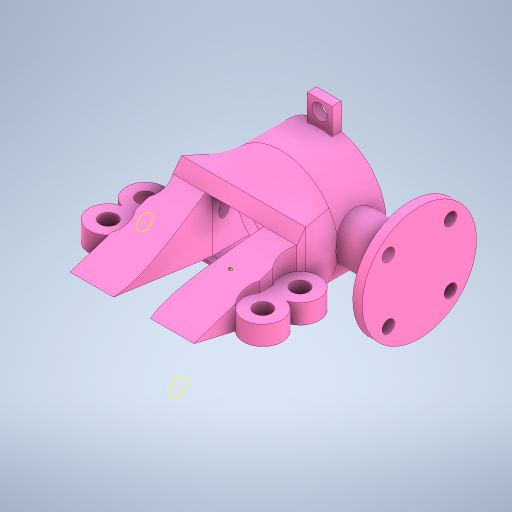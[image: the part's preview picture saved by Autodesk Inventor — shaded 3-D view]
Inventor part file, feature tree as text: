
AUTODESK INVENTOR PART (.ipt)
format: ipt  version: 2024 (Build 280153000, 153)  size: 1,857,024 bytes
history: native  units: mm
features: sketch x24, extrude x19, projected_geometry x11, split x10, other x10, loft x6, boolean_combine x5, plane x4, fillet x2, sweep x2, thicken_offset x2
ambient origin geometry x8: Origin, YZ Plane, XZ Plane, XY Plane, X Axis, Y Axis, Z Axis, Center Point
bodies: Solid1 (feature_tree), Solid2 (feature_tree), Solid19 (feature_tree), Solid20 (feature_tree), Solid21 (feature_tree), Solid22 (feature_tree), Solid23 (feature_tree), Solid3 (feature_tree), Solid4 (feature_tree), Solid5 (feature_tree), Solid6 (feature_tree), Solid7 (feature_tree), Solid8 (feature_tree), Solid9 (feature_tree), Solid10 (feature_tree), Solid11 (feature_tree), Solid12 (feature_tree), Solid13 (feature_tree), Solid14 (feature_tree), Solid15 (feature_tree), Solid16 (feature_tree), Solid17 (feature_tree), Solid18 (feature_tree)
feature tree (95):
  extrude  "Extrusion1"  Depth=3.0mm TaperAngle=0.0deg
  extrude  "Extrusion2"  Depth=3.0mm TaperAngle=0.0deg
  extrude  "Extrusion3"  Depth=40.0mm
  plane  "Work Plane2"
  sketch  "Sketch4"  dims[d4=29.0mm d5=3.0mm d6=0.0mm]
  loft  "Loft1"
  loft  "Loft2"
  loft  "Loft3"
  loft  "Loft4"
  boolean_combine  "Combine1"
  loft  "Loft5"
  fillet  "Fillet1"  [1 undecoded]
  fillet  "Fillet2"  [1 undecoded]
  plane  "Work Plane3"
  extrude  "Extrusion5"  TaperAngle=0.0deg  [1 undecoded]
  extrude  "Extrusion6"  TaperAngle=0.0deg  [1 undecoded]
  extrude  "Extrusion7"  Depth=40.0mm
  extrude  "Extrusion8"  TaperAngle=0.0deg  [1 undecoded]
  extrude  "Extrusion9"  Depth=2.0mm
  extrude  "Extrusion10"  Depth=38.0mm
  extrude  "Extrusion11"  Depth=3.0mm TaperAngle=0.0deg
  extrude  "Extrusion12"  Depth=3.0mm TaperAngle=0.0deg
  extrude  "Extrusion13"  Depth=12.5mm TaperAngle=0.0deg
  extrude  "Extrusion14"  Depth=3.7mm TaperAngle=0.0deg
  extrude  "Extrusion15"  Depth=8.5mm
  split  "Split1"
  split  "Split2"
  split  "Split3"
  split  "Split4"
  split  "Split5"
  split  "Split6"
  split  "Split7"
  boolean_combine  "Combine2"
  split  "Split8"
  boolean_combine  "Combine3"
  boolean_combine  "Combine4"
  extrude  "Extrusion16"  Depth=8.5mm
  extrude  "Extrusion17"  Depth=2.7mm TaperAngle=0.0deg
  sketch  "Sketch36"  dims[d47=15.0mm d48=3.0mm d49=0.0mm]
  sweep  "Sweep1"
  split  "Split9"
  loft  "Loft6"
  thicken_offset  "Thicken1"
  extrude  "Extrusion18"  Depth=10.0mm TaperAngle=0.0deg
  sweep  "Sweep2"
  split  "Split10"
  thicken_offset  "Thicken2"
  boolean_combine  "Combine5"
  plane  "Work Plane4"
  extrude  "Extrusion19"  Depth=10.0mm
  other  "Work Point1"
  other  "Work Point2"
  other  "Work Point3"
  extrude  "Extrusion20"  Depth=10.0mm
  sketch  "Sketch1"  dims[d0=3.0mm d1=0.0mm d2=9.5mm d3=0.0mm]
  plane  "Work Plane1"
  other  "2D Equation Curve1"
  other  "Edges1"
  other  "Edges2"
  other  "Edges3"
  other  "Edges4"
  sketch  "Sketch7"  dims[d7=12.0mm d8=36.0mm d9=40.0mm]
  sketch  "Sketch10"  dims[d10=9.0mm d11=10.0mm]
  sketch  "Sketch12"  dims[d12=3.0mm d13=-6.0mm d14=6.0mm]
  sketch  "Sketch13"  dims[d15=40.0mm d16=26.0mm]
  sketch  "Sketch16"  dims[d17=20.0mm d18=20.0mm]
  projected_geometry  "Projected Loop1"
  sketch  "Sketch18"  dims[d19=0.0mm d20=90.0deg d21=0.0mm d22=90.0deg d23=0.0mm d24=90.0deg d25=0.0mm d26=90.0deg]
  sketch  "Sketch19"  dims[d27=0.0mm d28=90.0deg d29=0.0mm d30=90.0deg]
  projected_geometry  "Projected Loop2"
  projected_geometry  "Projected Loop3"
  projected_geometry  "Projected Loop4"
  projected_geometry  "Projected Loop5"
  sketch  "Sketch23"  dims[d31=0.0mm d32=90.0deg d33=0.0mm d34=90.0deg]
  sketch  "Sketch24"  dims[d35=26.0mm d36=40.0mm]
  sketch  "Sketch28"  dims[d37=4.0mm d38=0.0mm d39=90.0deg]
  sketch  "Sketch29"  dims[d40=0.0mm d41=90.0deg d42=2.0mm]
  sketch  "Sketch35"  dims[d43=1.5mm d46=38.0mm]
  projected_geometry  "Projected Loop11"
  sketch  "3D Sketch2"
  other  "Srf1"
  sketch  "Sketch38"  dims[d50=15.0mm d51=3.0mm d52=0.0mm]
  projected_geometry  "Projected Loop12"
  sketch  "Sketch42"  dims[d53=11.0mm d54=12.5mm d55=0.0mm]
  projected_geometry  "Projected Loop19"
  projected_geometry  "Projected Loop20"
  sketch  "Sketch43"  dims[d56=11.0mm d57=3.7mm d58=0.0mm]
  sketch  "Sketch46"  dims[d59=20.0mm d60=0.0mm d61=8.5mm]
  projected_geometry  "Projected Loop21"
  sketch  "3D Sketch3"
  sketch  "Sketch47"  dims[d62=8.5mm d63=8.5mm]
  projected_geometry  "Projected Loop22"
  sketch  "Sketch49"  dims[d64=8.5mm d65=2.7mm d66=0.0mm]
  sketch  "Sketch50"  dims[d67=40.0mm d68=10.0mm d69=2.7mm d70=0.0mm d71=2.5mm d72=0.0mm d73=2.5mm d74=0.0mm d75=9.0mm d76=2.0mm d77=0.0mm d78=0.0mm d79=7.0mm d80=5.5mm d81=8.5mm d82=8.5mm d83=2.5mm d84=0.0mm d85=2.5mm d86=0.0mm d87=0.5mm d88=0.0mm d89=0.0mm d91=10.0mm d92=10.0mm d93=0.1mm d94=0.0mm d95=16.0mm d96=2.5mm d97=4.0mm d98=2.5mm d99=2.5mm d100=5.0mm d101=5.0mm d102=2.5mm d103=2.5mm d104=2.5mm d105=2.5mm d106=0.0mm d107=0.0mm d108=2.5mm d109=2.5mm d110=0.0mm d111=90.0deg d112=0.0mm d113=90.0deg d114=0.1mm d115=0.1mm d116=0.1mm d117=0.0mm d118=15.0mm d119=3.0mm d120=1.6mm d121=1.5mm d122=16.5mm d125=5.5mm d126=2.5mm d127=2.5mm d128=0.0mm d129=0.0mm d130=0.1mm d131=0.1mm d132=58.25mm d133=6.0mm d134=16.0mm d135=0.0mm d136=12.0mm d137=12.0mm d138=12.0mm d139=12.0mm d140=10.0mm d141=0.0mm]
  other  "Unwrap1"
note: 5 required parameter values undecoded (feature->parameter linkage not recoverable at this tier; creation-order binding heuristic only, values carry confidence <= 0.55)
